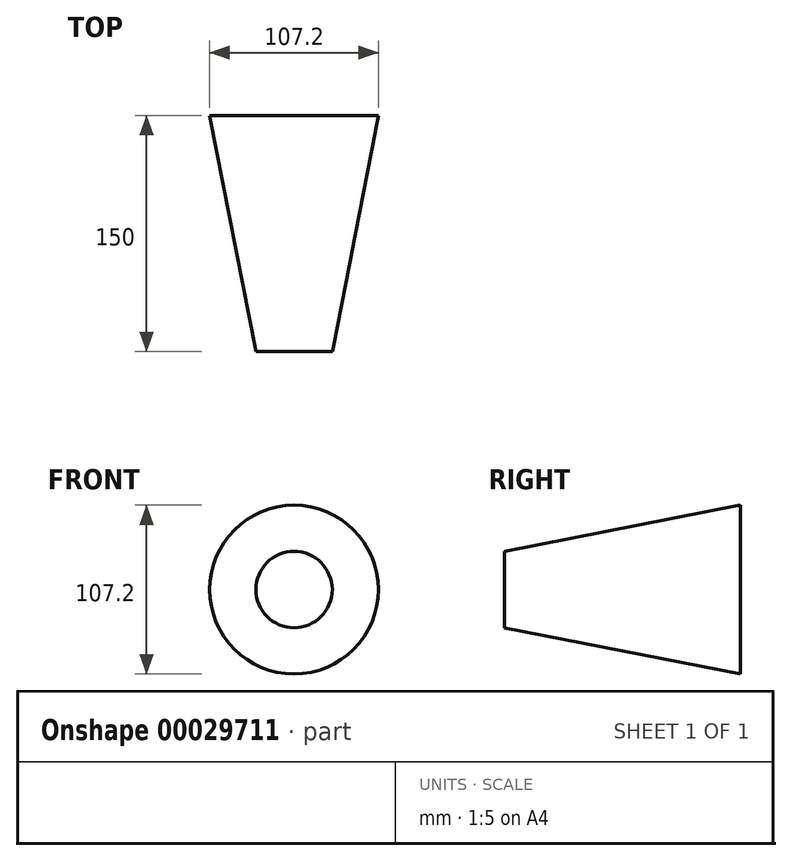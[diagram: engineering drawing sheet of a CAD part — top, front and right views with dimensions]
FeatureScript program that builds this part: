
annotation { "Feature Type Name" : "Feature", "Feature Type Description" : "" }
export const myFeature = defineFeature(function(context is Context, id is Id, definition is map)
    precondition{}
    {
        {
            var Q0;
            Q0=qCreatedBy(makeId("Front.planeOp"),FACE);
            var sketch = newSketch(context, id + "F0", { "sketchPlane" : qUnion([Q0])});
            skCircle(sketch, "E0", {"center": v(0, 0) * mm, "radius": 57.3 * mm});
            skCircle(sketch, "E1", {"center": v(0, 0) * mm, "radius": 53.6 * mm});
            skSolve(sketch);
        }
        {
            var Q0;
            Q0=qCreatedBy(makeId("Front.planeOp"),FACE);
            cPlane(context, id + "F1", {"entities" : qUnion([Q0]), "cplaneType" : CPlaneType.OFFSET, "offset" : 150 * mm, "width" : 150 * mm, "height" : 150 * mm});
        }
        {
            var Q0;
            Q0=qCreatedBy(id+"F1.planeOp",FACE);
            var sketch = newSketch(context, id + "F2", { "sketchPlane" : qUnion([Q0])});
            skCircle(sketch, "E2", {"center": v(0, 0) * mm, "radius": 24.28 * mm});
            skCircle(sketch, "E3", {"center": v(0, 0) * mm, "radius": 27.06 * mm});
            skSolve(sketch);
        }
        {
            var Q0;
            Q0=makeQuery(id+"F0.imprint","IMPRINT",FACE,{"disambiguationData":[TD([[makeQuery(id+"F0.imprint","IMPRINT",EDGE,{"derivedFrom":sQuery(id+"F0.wireOp",EDGE,"E0")}),1.0]])]});
            var Q1;
            Q1=makeQuery(id+"F2.imprint","IMPRINT",FACE,{"disambiguationData":[TD([[makeQuery(id+"F2.imprint","IMPRINT",EDGE,{"derivedFrom":sQuery(id+"F2.wireOp",EDGE,"E2")}),1.0]])]});
            var Q2;
            Q2=makeQuery(id+"F0.imprint","IMPRINT",FACE,{"disambiguationData":[TD([[makeQuery(id+"F0.imprint","IMPRINT",EDGE,{"derivedFrom":sQuery(id+"F0.wireOp",EDGE,"E1")}),1.0]])]});
            var Q3;
            Q3=sQuery(id+"F2.wireOp",EDGE,"E2");
            loft(context, id + "F3", {"bodyType" : ToolBodyType.SURFACE, "operationType" : NewBodyOperationType.INTERSECT, "sheetProfilesArray" : [{ "sheetProfileEntities" : qUnion([Q0]) }, { "sheetProfileEntities" : qUnion([Q1]) }], "wireProfilesArray" : [{ "wireProfileEntities" : qUnion([Q2]) }, { "wireProfileEntities" : qUnion([Q3]) }]});
        }
    });
